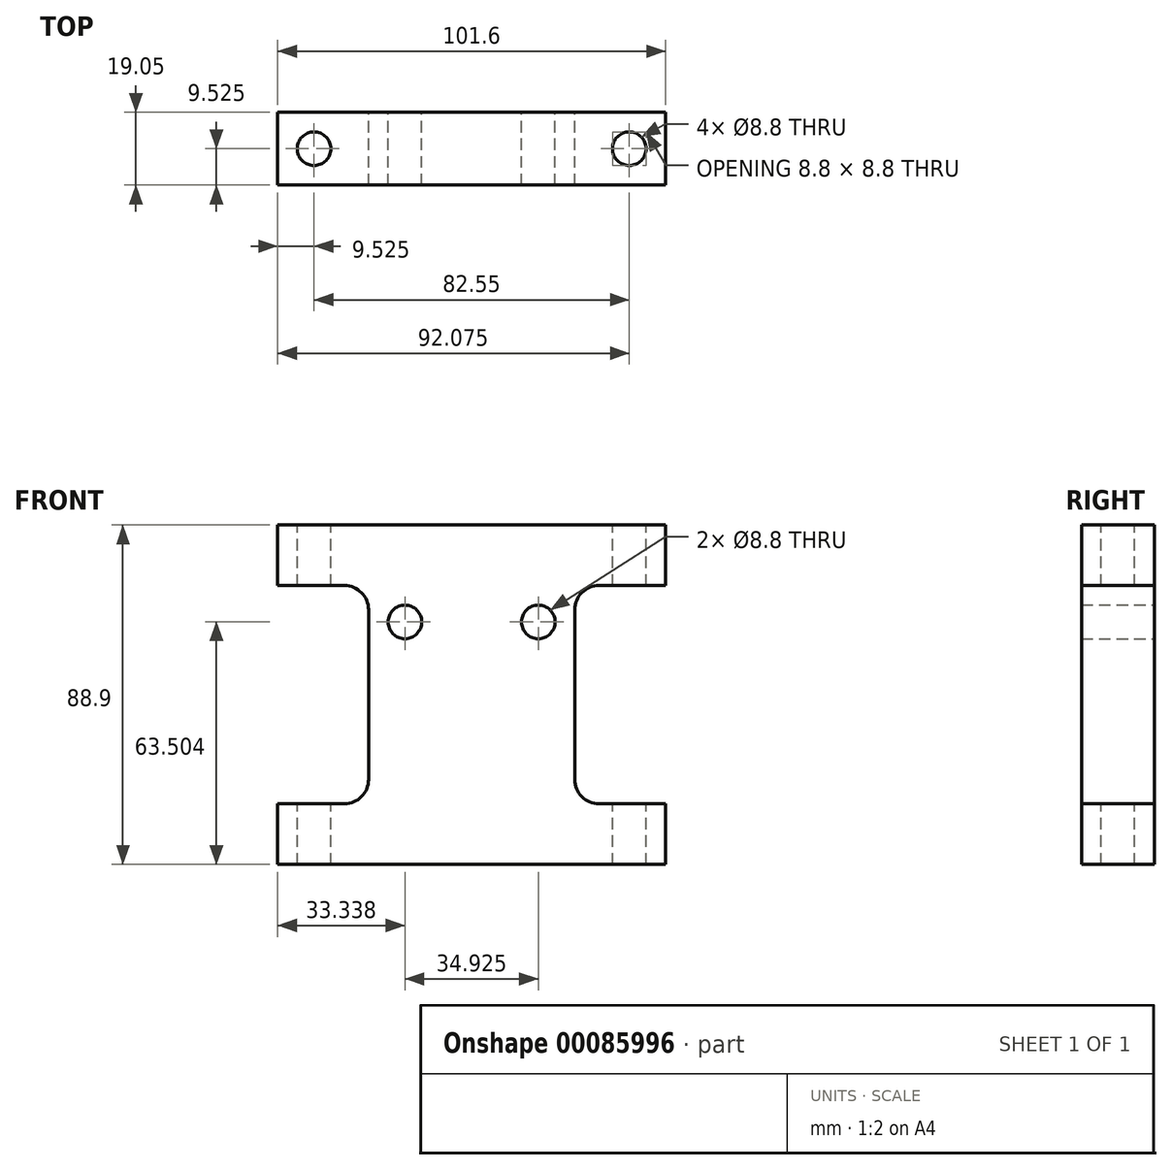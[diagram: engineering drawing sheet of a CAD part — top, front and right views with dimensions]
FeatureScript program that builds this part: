
annotation { "Feature Type Name" : "Feature", "Feature Type Description" : "" }
export const myFeature = defineFeature(function(context is Context, id is Id, definition is map)
    precondition{}
    {
        {
            var Q0;
            Q0=qCreatedBy(makeId("Front.planeOp"),FACE);
            var sketch = newSketch(context, id + "F0", { "sketchPlane" : qUnion([Q0])});
            skLineSegment(sketch, "E0", {"start": v(-47.02, 51) * mm, "end": v(54.58, 51) * mm});
            skLineSegment(sketch, "E1", {"start": v(-47.02, 51) * mm, "end": v(-47.02, 35.12) * mm});
            skLineSegment(sketch, "E2", {"start": v(3.78, 51) * mm, "end": v(3.78, 6.54) * mm, "construction": true});
            skLineSegment(sketch, "E3", {"start": v(3.78, 35.12) * mm, "end": v(-23.2, 35.12) * mm, "construction": true});
            skLineSegment(sketch, "E4", {"start": v(-23.2, 35.12) * mm, "end": v(-23.2, 6.54) * mm});
            skLineSegment(sketch, "E5", {"start": v(-47.02, 35.12) * mm, "end": v(-23.2, 35.12) * mm});
            skLineSegment(sketch, "E6", {"start": v(-23.2, 6.54) * mm, "end": v(3.78, 6.54) * mm, "construction": true});
            skLineSegment(sketch, "E7.MirrorCS", {"start": v(54.58, 51) * mm, "end": v(54.58, 35.12) * mm});
            skLineSegment(sketch, "E8.MirrorCS", {"start": v(54.58, 35.12) * mm, "end": v(30.77, 35.12) * mm});
            skLineSegment(sketch, "E9.MirrorCS", {"start": v(30.77, 35.12) * mm, "end": v(30.77, 6.54) * mm});
            skLineSegment(sketch, "E10.MirrorCS", {"start": v(30.77, 6.54) * mm, "end": v(3.78, 6.54) * mm, "construction": true});
            skLineSegment(sketch, "E11.MirrorCS", {"start": v(30.77, -22.03) * mm, "end": v(30.77, 6.54) * mm});
            skLineSegment(sketch, "E12.MirrorCS", {"start": v(54.58, -22.03) * mm, "end": v(30.77, -22.03) * mm});
            skLineSegment(sketch, "E13.MirrorCS", {"start": v(54.58, -37.9) * mm, "end": v(54.58, -22.03) * mm});
            skLineSegment(sketch, "E14.MirrorCS", {"start": v(-47.02, -37.9) * mm, "end": v(54.58, -37.9) * mm});
            skLineSegment(sketch, "E15.MirrorCS", {"start": v(-47.02, -37.9) * mm, "end": v(-47.02, -22.03) * mm});
            skLineSegment(sketch, "E16.MirrorCS", {"start": v(-47.02, -22.03) * mm, "end": v(-23.2, -22.03) * mm});
            skLineSegment(sketch, "E17.MirrorCS", {"start": v(-23.2, -22.03) * mm, "end": v(-23.2, 6.54) * mm});
            skLineSegment(sketch, "E18", {"start": v(3.78, 51) * mm, "end": v(3.78, 31.94) * mm});
            skLineSegment(sketch, "E19.MirrorCS", {"start": v(3.78, -37.9) * mm, "end": v(3.78, -18.86) * mm, "construction": true});
            skLineSegment(sketch, "E20", {"start": v(-23.2, 51) * mm, "end": v(-23.2, 25.6) * mm, "construction": true});
            skLineSegment(sketch, "E21", {"start": v(-23.2, 25.6) * mm, "end": v(-13.68, 25.6) * mm, "construction": true});
            skLineSegment(sketch, "E22.MirrorCS", {"start": v(30.77, 25.6) * mm, "end": v(21.24, 25.6) * mm, "construction": true});
            skLineSegment(sketch, "E23.MirrorCS", {"start": v(30.77, 51) * mm, "end": v(30.77, 25.6) * mm, "construction": true});
            skSolve(sketch);
        }
        {
            var Q0;
            {var subQ1=sQuery(id+"F0.wireOp",EDGE,"E1");Q0=makeQuery(id+"F0.imprint","IMPRINT",FACE,{"disambiguationData":[TD([[makeQuery(id+"F0.imprint","IMPRINT",EDGE,{"derivedFrom":subQ1}),1.0]])]});}
            var Q1;
            {var subQ0=sQuery(id+"F0.wireOp",EDGE,"E7.MirrorCS");Q1=makeQuery(id+"F0.imprint","IMPRINT",FACE,{"disambiguationData":[TD([[makeQuery(id+"F0.imprint","IMPRINT",EDGE,{"derivedFrom":subQ0}),-1.0]])]});}
            var Q2;
            Q2=makeQuery(id+"F0.imprint","IMPRINT",FACE,{"disambiguationData":[TD([[makeQuery(id+"F0.imprint","IMPRINT",EDGE,{"derivedFrom":sQuery(id+"F0.wireOp",EDGE,"E6")}),-1.0]])]});
            var Q3;
            {var subQ1=sQuery(id+"F0.wireOp",EDGE,"E4");Q3=makeQuery(id+"F0.imprint","IMPRINT",FACE,{"disambiguationData":[TD([[makeQuery(id+"F0.imprint","IMPRINT",EDGE,{"derivedFrom":subQ1}),1.0]])]});}
            extrude(context, id + "F1", {"entities" : qUnion([Q0, Q1, Q2, Q3]), "depth" : 19.05 * mm});
        }
        {
            var Q0;
            Q0=makeQuery(id+"F1.opExtrude","SWEPT_EDGE",EDGE,{"disambiguationData":[OSD([sQuery(id+"F0.wireOp",EDGE,"E11.MirrorCS"),sQuery(id+"F0.wireOp",EDGE,"E12.MirrorCS")])]});
            var Q1;
            Q1=makeQuery(id+"F1.opExtrude","SWEPT_EDGE",EDGE,{"disambiguationData":[OSD([sQuery(id+"F0.wireOp",EDGE,"E8.MirrorCS"),sQuery(id+"F0.wireOp",EDGE,"E9.MirrorCS")])]});
            var Q2;
            Q2=makeQuery(id+"F1.opExtrude","SWEPT_EDGE",EDGE,{"disambiguationData":[OSD([sQuery(id+"F0.wireOp",EDGE,"E16.MirrorCS"),sQuery(id+"F0.wireOp",EDGE,"E17.MirrorCS")])]});
            var Q3;
            Q3=makeQuery(id+"F1.opExtrude","SWEPT_EDGE",EDGE,{"disambiguationData":[OSD([sQuery(id+"F0.wireOp",EDGE,"E3"),sQuery(id+"F0.wireOp",EDGE,"E4"),sQuery(id+"F0.wireOp",EDGE,"E5")])]});
            fillet(context, id + "F2", {"entities" : qUnion([Q0, Q1, Q2, Q3]), "radius" : 6.35 * mm, "tangentPropagation" : true, "allowEdgeOverflow" : false});
        }
        {
            var Q0;
            Q0=makeQuery(id+"F1.opExtrude","SWEPT_FACE",FACE,{"disambiguationData":[OSD([sQuery(id+"F0.wireOp",EDGE,"E0")])]});
            var sketch = newSketch(context, id + "F3", { "sketchPlane" : qUnion([Q0])});
            skLineSegment(sketch, "E24", {"start": v(3.78, -9.53) * mm, "end": v(45.06, -9.53) * mm});
            skPoint(sketch, "E24.startSnap0", {"position": v(54.58, -9.53) * mm});
            skPoint(sketch, "E24.startSnap1", {"position": v(3.78, -19.05) * mm});
            skLineSegment(sketch, "E25", {"start": v(45.06, -9.53) * mm, "end": v(-37.5, -9.53) * mm});
            skSolve(sketch);
        }
        {
            var Q0;
            Q0=sQuery(id+"F3.wireOp",VERTEX,"E25.end");
            var Q1;
            Q1=sQuery(id+"F3.wireOp",VERTEX,"E25.start");
            var Q2;
            Q2=makeQuery(id+"F1.opExtrude","SWEPT_BODY",BODY,{"disambiguationData":[OSD([sQuery(id+"F0.wireOp",EDGE,"E0"),sQuery(id+"F0.wireOp",EDGE,"E1"),sQuery(id+"F0.wireOp",EDGE,"E4"),sQuery(id+"F0.wireOp",EDGE,"E5"),sQuery(id+"F0.wireOp",EDGE,"E7.MirrorCS"),sQuery(id+"F0.wireOp",EDGE,"E8.MirrorCS"),sQuery(id+"F0.wireOp",EDGE,"E9.MirrorCS"),sQuery(id+"F0.wireOp",EDGE,"E11.MirrorCS"),sQuery(id+"F0.wireOp",EDGE,"E12.MirrorCS"),sQuery(id+"F0.wireOp",EDGE,"E13.MirrorCS"),sQuery(id+"F0.wireOp",EDGE,"E14.MirrorCS"),sQuery(id+"F0.wireOp",EDGE,"E15.MirrorCS"),sQuery(id+"F0.wireOp",EDGE,"E16.MirrorCS"),sQuery(id+"F0.wireOp",EDGE,"E17.MirrorCS"),sQuery(id+"F0.wireOp",EDGE,"b822ef5e-f759-4389-9a1f-4495ec9d3cc8"),sQuery(id+"F0.wireOp",EDGE,"e4bdc8b9-5a86-444b-bff0-bdd0d70382300.MirrorC")])]});
            hole(context, id + "F4", {"style" : HoleStyle.SIMPLE, "endStyle" : HoleEndStyle.THROUGH, "standardTappedOrClearance" : lookupTablePath({ "standard" : "ISO", "fit" : "Normal", "size" : "M8", "type" : "Clearance" }), "standardBlindInLast" : lookupTablePath({ "fit" : "Standard", "standard" : "ISO", "size" : "M8", "type" : "Clearance" }), "holeDiameter" : 8.8 * mm, "locations" : qUnion([Q0, Q1]), "scope" : qUnion([Q2]), "isTappedThrough" : true});
        }
        {
            var Q0;
            Q0=sQuery(id+"F0.wireOp",VERTEX,"E21.end");
            var Q1;
            Q1=sQuery(id+"F0.wireOp",VERTEX,"E22.MirrorCS.end");
            var Q2;
            Q2=makeQuery(id+"F1.opExtrude","SWEPT_BODY",BODY,{"disambiguationData":[OSD([sQuery(id+"F0.wireOp",EDGE,"E0"),sQuery(id+"F0.wireOp",EDGE,"E1"),sQuery(id+"F0.wireOp",EDGE,"E4"),sQuery(id+"F0.wireOp",EDGE,"E5"),sQuery(id+"F0.wireOp",EDGE,"E7.MirrorCS"),sQuery(id+"F0.wireOp",EDGE,"E8.MirrorCS"),sQuery(id+"F0.wireOp",EDGE,"E9.MirrorCS"),sQuery(id+"F0.wireOp",EDGE,"E11.MirrorCS"),sQuery(id+"F0.wireOp",EDGE,"E12.MirrorCS"),sQuery(id+"F0.wireOp",EDGE,"E13.MirrorCS"),sQuery(id+"F0.wireOp",EDGE,"E14.MirrorCS"),sQuery(id+"F0.wireOp",EDGE,"E15.MirrorCS"),sQuery(id+"F0.wireOp",EDGE,"E16.MirrorCS"),sQuery(id+"F0.wireOp",EDGE,"E17.MirrorCS")])]});
            hole(context, id + "F5", {"style" : HoleStyle.SIMPLE, "endStyle" : HoleEndStyle.THROUGH, "oppositeDirection" : true, "standardTappedOrClearance" : lookupTablePath({ "standard" : "ISO", "fit" : "Normal", "size" : "M8", "type" : "Clearance" }), "standardBlindInLast" : lookupTablePath({ "fit" : "Standard", "standard" : "ISO", "size" : "M8", "type" : "Clearance" }), "holeDiameter" : 8.8 * mm, "locations" : qUnion([Q0, Q1]), "scope" : qUnion([Q2]), "isTappedThrough" : true});
        }
    });
